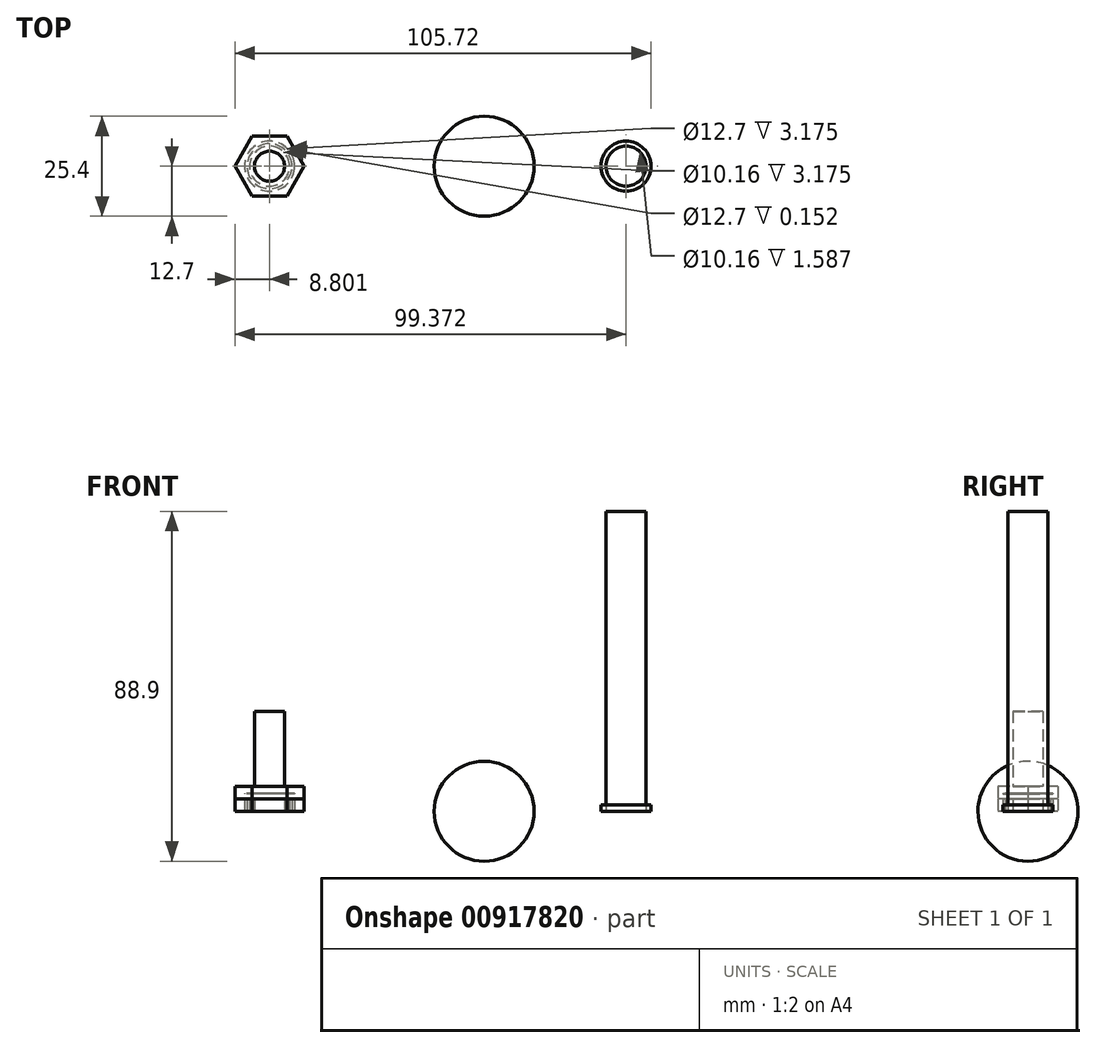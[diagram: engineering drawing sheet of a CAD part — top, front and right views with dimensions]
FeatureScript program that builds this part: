
annotation { "Feature Type Name" : "Feature", "Feature Type Description" : "" }
export const myFeature = defineFeature(function(context is Context, id is Id, definition is map)
    precondition{}
    {
        {
            var Q0;
            Q0=qCreatedBy(makeId("Top.planeOp"),FACE);
            var sketch = newSketch(context, id + "F0", { "sketchPlane" : qUnion([Q0])});
            skCircle(sketch, "E0", {"center": v(0, 0) * mm, "radius": 12.7 * mm});
            skCircle(sketch, "E1.cCircle", {"center": v(-54.54, 0) * mm, "radius": 7.62 * mm, "construction": true});
            skLineSegment(sketch, "E1.0", {"start": v(-50.14, -7.62) * mm, "end": v(-58.94, -7.62) * mm});
            skLineSegment(sketch, "E1.1", {"start": v(-58.94, -7.62) * mm, "end": v(-63.34, 0) * mm});
            skLineSegment(sketch, "E1.2", {"start": v(-63.34, 0) * mm, "end": v(-58.94, 7.62) * mm});
            skLineSegment(sketch, "E1.3", {"start": v(-58.94, 7.62) * mm, "end": v(-50.14, 7.62) * mm});
            skLineSegment(sketch, "E1.4", {"start": v(-50.14, 7.62) * mm, "end": v(-45.74, 0) * mm});
            skLineSegment(sketch, "E1.5", {"start": v(-45.74, 0) * mm, "end": v(-50.14, -7.62) * mm});
            skPoint(sketch, "E1.0.midPoint", {"position": v(-54.54, -7.62) * mm});
            skCircle(sketch, "E2", {"center": v(36.03, 0) * mm, "radius": 6.35 * mm});
            skCircle(sketch, "E3", {"center": v(-54.54, 0) * mm, "radius": 6.35 * mm});
            skCircle(sketch, "E4", {"center": v(-54.54, 0) * mm, "radius": 5.08 * mm});
            skLineSegment(sketch, "E5", {"start": v(0, 12.7) * mm, "end": v(0, -12.7) * mm});
            skCircle(sketch, "E6", {"center": v(36.03, 0) * mm, "radius": 5.08 * mm});
            skSolve(sketch);
        }
        {
            var Q0;
            Q0=qCreatedBy(makeId("Top.planeOp"),FACE);
            var sketch = newSketch(context, id + "F1", { "sketchPlane" : qUnion([Q0])});
            skCircle(sketch, "E7.0", {"center": v(-54.54, 0) * mm, "radius": 3.81 * mm});
            skCircle(sketch, "E7.1", {"center": v(-54.54, 0) * mm, "radius": 5.08 * mm});
            skSolve(sketch);
        }
        {
            var Q0;
            {var subQ0=sQuery(id+"F0.wireOp",EDGE,"E5");Q0=makeQuery(id+"F0.imprint","IMPRINT",FACE,{"disambiguationData":[TD([[makeQuery(id+"F0.imprint","IMPRINT",EDGE,{"derivedFrom":subQ0}),1.0]])]});}
            var Q1;
            Q1=sQuery(id+"F0.wireOp",EDGE,"E5");
            revolve(context, id + "F2", {"surfaceOperationType" : NewSurfaceOperationType.NEW, "entities" : qUnion([Q0]), "axis" : qUnion([Q1]), "revolveType" : RevolveType.FULL});
        }
        {
            var Q0;
            Q0=makeQuery(id+"F0.imprint","IMPRINT",FACE,{"disambiguationData":[TD([[makeQuery(id+"F0.imprint","IMPRINT",EDGE,{"derivedFrom":sQuery(id+"F0.wireOp",EDGE,"E1.0")}),-1.0]])]});
            var Q1;
            Q1=makeQuery(id+"F1.imprint","IMPRINT",FACE,{"disambiguationData":[TD([[makeQuery(id+"F1.imprint","IMPRINT",EDGE,{"derivedFrom":sQuery(id+"F1.wireOp",EDGE,"E7.0")}),-1.0]])]});
            extrude(context, id + "F3", {"entities" : qUnion([Q0, Q1]), "depth" : 3.17 * mm, "offsetDistance" : 25.4 * mm});
        }
        {
            var Q0;
            Q0=qCreatedBy(makeId("Top.planeOp"),FACE);
            var sketch = newSketch(context, id + "F4", { "sketchPlane" : qUnion([Q0])});
            skCircle(sketch, "E8", {"center": v(-54.54, 0) * mm, "radius": 5.72 * mm});
            skCircle(sketch, "E9.0", {"center": v(-54.54, 0) * mm, "radius": 5.08 * mm});
            skSolve(sketch);
        }
        {
            var Q0;
            Q0=makeQuery(id+"F3.opExtrude","CAP_FACE",FACE,{"disambiguationData":[OSD([sQuery(id+"F1.wireOp",EDGE,"E7.0"),sQuery(id+"F1.wireOp",EDGE,"E7.1")])],"isStart":false});
            extrude(context, id + "F5", {"entities" : qUnion([Q0]), "operationType" : NewBodyOperationType.REMOVE, "oppositeDirection" : true, "depth" : 4.37 * mm, "offsetDistance" : 25.4 * mm});
        }
        {
            var Q0;
            Q0 = qSketchRegion(id + "F4", true);
            extrude(context, id + "F6", {"entities" : qUnion([Q0]), "depth" : 4.44 * mm, "offsetDistance" : 25.4 * mm});
        }
        {
            var Q0;
            Q0=makeQuery(id+"F3.opExtrude","CAP_FACE",FACE,{"disambiguationData":[OSD([sQuery(id+"F0.wireOp",EDGE,"E1.0"),sQuery(id+"F0.wireOp",EDGE,"E1.1"),sQuery(id+"F0.wireOp",EDGE,"E1.2"),sQuery(id+"F0.wireOp",EDGE,"E1.3"),sQuery(id+"F0.wireOp",EDGE,"E1.4"),sQuery(id+"F0.wireOp",EDGE,"E1.5"),sQuery(id+"F0.wireOp",EDGE,"E3")])],"isStart":false});
            var sketch = newSketch(context, id + "F7", { "sketchPlane" : qUnion([Q0])});
            skCircle(sketch, "E10", {"center": v(-54.54, 0) * mm, "radius": 3.81 * mm});
            skSolve(sketch);
        }
        {
            var Q0;
            Q0=makeQuery(id+"F7.imprint","IMPRINT",FACE,{"disambiguationData":[TD([[makeQuery(id+"F7.imprint","IMPRINT",EDGE,{"derivedFrom":sQuery(id+"F7.wireOp",EDGE,"E10")}),-1.0]])]});
            extrude(context, id + "F8", {"entities" : qUnion([Q0]), "operationType" : NewBodyOperationType.ADD, "depth" : 1.27 * mm, "offsetDistance" : 25.4 * mm});
        }
        {
            var Q0;
            Q0=makeQuery(id+"F3.opExtrude","CAP_FACE",FACE,{"disambiguationData":[OSD([sQuery(id+"F0.wireOp",EDGE,"E1.0"),sQuery(id+"F0.wireOp",EDGE,"E1.1"),sQuery(id+"F0.wireOp",EDGE,"E1.2"),sQuery(id+"F0.wireOp",EDGE,"E1.3"),sQuery(id+"F0.wireOp",EDGE,"E1.4"),sQuery(id+"F0.wireOp",EDGE,"E1.5"),sQuery(id+"F0.wireOp",EDGE,"E3")])],"isStart":false});
            extrude(context, id + "F9", {"entities" : qUnion([Q0]), "depth" : 3.17 * mm, "offsetDistance" : 25.4 * mm});
        }
        {
            var Q0;
            {var subQ0=sQuery(id+"F4.wireOp",EDGE,"E8");Q0=makeQuery(id+"F8.boolean.opBoolean","MERGE",FACE,{"derivedFrom":[makeQuery(id+"F6.opExtrude","CAP_FACE",FACE,{"disambiguationData":[OSD([subQ0,sQuery(id+"F4.wireOp",EDGE,"E9.0")])],"isStart":false}),makeQuery(id+"F8.opExtrude","CAP_FACE",FACE,{"disambiguationData":[OSD([sQuery(id+"F0.wireOp",EDGE,"E1.0"),sQuery(id+"F0.wireOp",EDGE,"E1.1"),sQuery(id+"F0.wireOp",EDGE,"E1.2"),sQuery(id+"F0.wireOp",EDGE,"E1.3"),sQuery(id+"F0.wireOp",EDGE,"E1.4"),sQuery(id+"F0.wireOp",EDGE,"E1.5"),sQuery(id+"F0.wireOp",EDGE,"E3"),subQ0,sQuery(id+"F7.wireOp",EDGE,"E10")])],"isStart":false})]});}
            extrude(context, id + "F10", {"entities" : qUnion([Q0]), "operationType" : NewBodyOperationType.ADD, "depth" : 1.9 * mm, "offsetDistance" : 25.4 * mm, "hasSecondDirection" : true, "secondDirectionOppositeDirection" : false, "secondDirectionDepth" : 0.15 * mm});
        }
        {
            var Q0;
            Q0=makeQuery(id+"F0.imprint","IMPRINT",FACE,{"disambiguationData":[TD([[makeQuery(id+"F0.imprint","IMPRINT",EDGE,{"derivedFrom":sQuery(id+"F0.wireOp",EDGE,"E2")}),1.0]])]});
            extrude(context, id + "F11", {"entities" : qUnion([Q0]), "depth" : 1.59 * mm, "offsetDistance" : 25.4 * mm});
        }
        {
            var Q0;
            Q0=makeQuery(id+"F0.imprint","IMPRINT",FACE,{"disambiguationData":[TD([[makeQuery(id+"F0.imprint","IMPRINT",EDGE,{"derivedFrom":sQuery(id+"F0.wireOp",EDGE,"E6")}),1.0]])]});
            extrude(context, id + "F12", {"entities" : qUnion([Q0]), "depth" : 76.2 * mm, "offsetDistance" : 25.4 * mm});
        }
        {
            var Q0;
            Q0=makeQuery(id+"F1.imprint","IMPRINT",FACE,{"disambiguationData":[TD([[makeQuery(id+"F1.imprint","IMPRINT",EDGE,{"derivedFrom":sQuery(id+"F1.wireOp",EDGE,"E7.0")}),1.0]])]});
            var Q1;
            Q1=sQuery(id+"F1.wireOp",EDGE,"E7.0");
            extrude(context, id + "F13", {"entities" : qUnion([Q0]), "operationType" : NewBodyOperationType.ADD, "surfaceEntities" : qUnion([Q1]), "depth" : 25.4 * mm, "offsetDistance" : 25.4 * mm});
        }
        {
            var Q0;
            Q0=qCreatedBy(makeId("Top.planeOp"),FACE);
            cPlane(context, id + "F14", {"entities" : qUnion([Q0]), "cplaneType" : CPlaneType.OFFSET, "offset" : 3.17 * mm, "width" : 152.4 * mm, "height" : 152.4 * mm});
        }
    });
